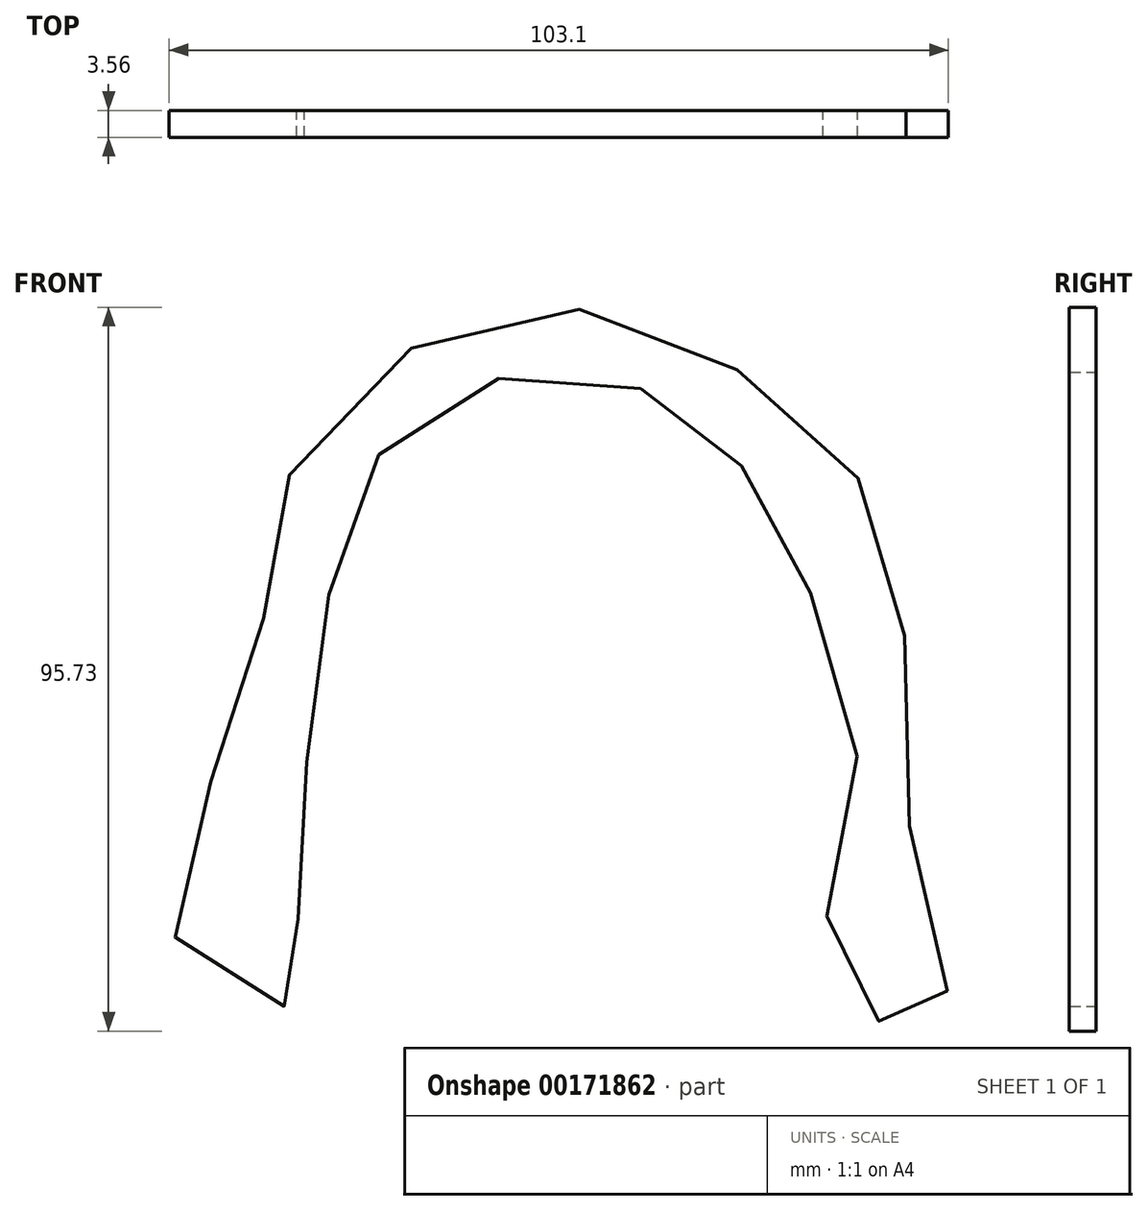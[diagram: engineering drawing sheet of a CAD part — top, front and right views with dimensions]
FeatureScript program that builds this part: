
annotation { "Feature Type Name" : "Feature", "Feature Type Description" : "" }
export const myFeature = defineFeature(function(context is Context, id is Id, definition is map)
    precondition{}
    {
        {
            var Q0;
            Q0=qCreatedBy(makeId("Front.planeOp"),FACE);
            var sketch = newSketch(context, id + "F0", { "sketchPlane" : qUnion([Q0])});
            skFitSpline(sketch, "E0", {"points": [v(-41.7, -14.35) * mm, v(-42.3, -25.59) * mm, v(-57.97, -16.71) * mm, v(-47.92, 16.12) * mm, v(-43.48, 43.04) * mm, v(-15.38, 65.81) * mm, v(17.16, 57.83) * mm, v(36.97, 34.46) * mm, v(39.93, -6.95) * mm, v(43.18, -28.54) * mm, v(28.99, -22.92) * mm, v(32.24, 2.8) * mm, v(23.07, 35.05) * mm, v(10.94, 51.91) * mm, v(-11.24, 57.83) * mm, v(-31.94, 45.7) * mm, v(-39.04, 17.3) * mm, v(-41.7, -14.35) * mm]});
            skSolve(sketch);
        }
        {
            var Q0;
            Q0 = qSketchRegion(id + "F0", true);
            extrude(context, id + "F1", {"entities" : qUnion([Q0]), "depth" : 3.56 * mm});
        }
    });
